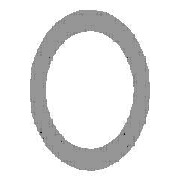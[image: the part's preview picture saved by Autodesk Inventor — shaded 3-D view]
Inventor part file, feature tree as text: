
AUTODESK INVENTOR PART (.ipt)
format: ipt  version: 2013 (Build 170138000, 138)  size: 114,688 bytes
history: native  units: mm (DEFAULTED — no unit token found)
features: other x4, sketch x3, plane x2, split x1
ambient origin geometry x8: Origin, YZ Plane, XZ Plane, XY Plane, X Axis, Y Axis, Z Axis, Center Point
bodies: Solid1 (feature_tree), Body (feature_tree)
feature tree (10):
  parser-record x1  (decoder bookkeeping rows leaked as tree rows — omitted from the tree; the rows remain in map.json)
  other  "Driven Length"
  other  "Start plane"
  other  "End plane"
  plane  "Work Plane4"
  split  "Split1"
  sketch  "Sketch"  dims[d2=258.474886mm d3=0.0mm d4=-4.474886mm d5=254.0mm d6=90.0deg d7=258.474886mm]
  sketch  "Sketch3"  dims[d0=33.401mm]
  plane  "Work Plane3"
  sketch  "Sketch4"  dims[d1=3.3782mm]
